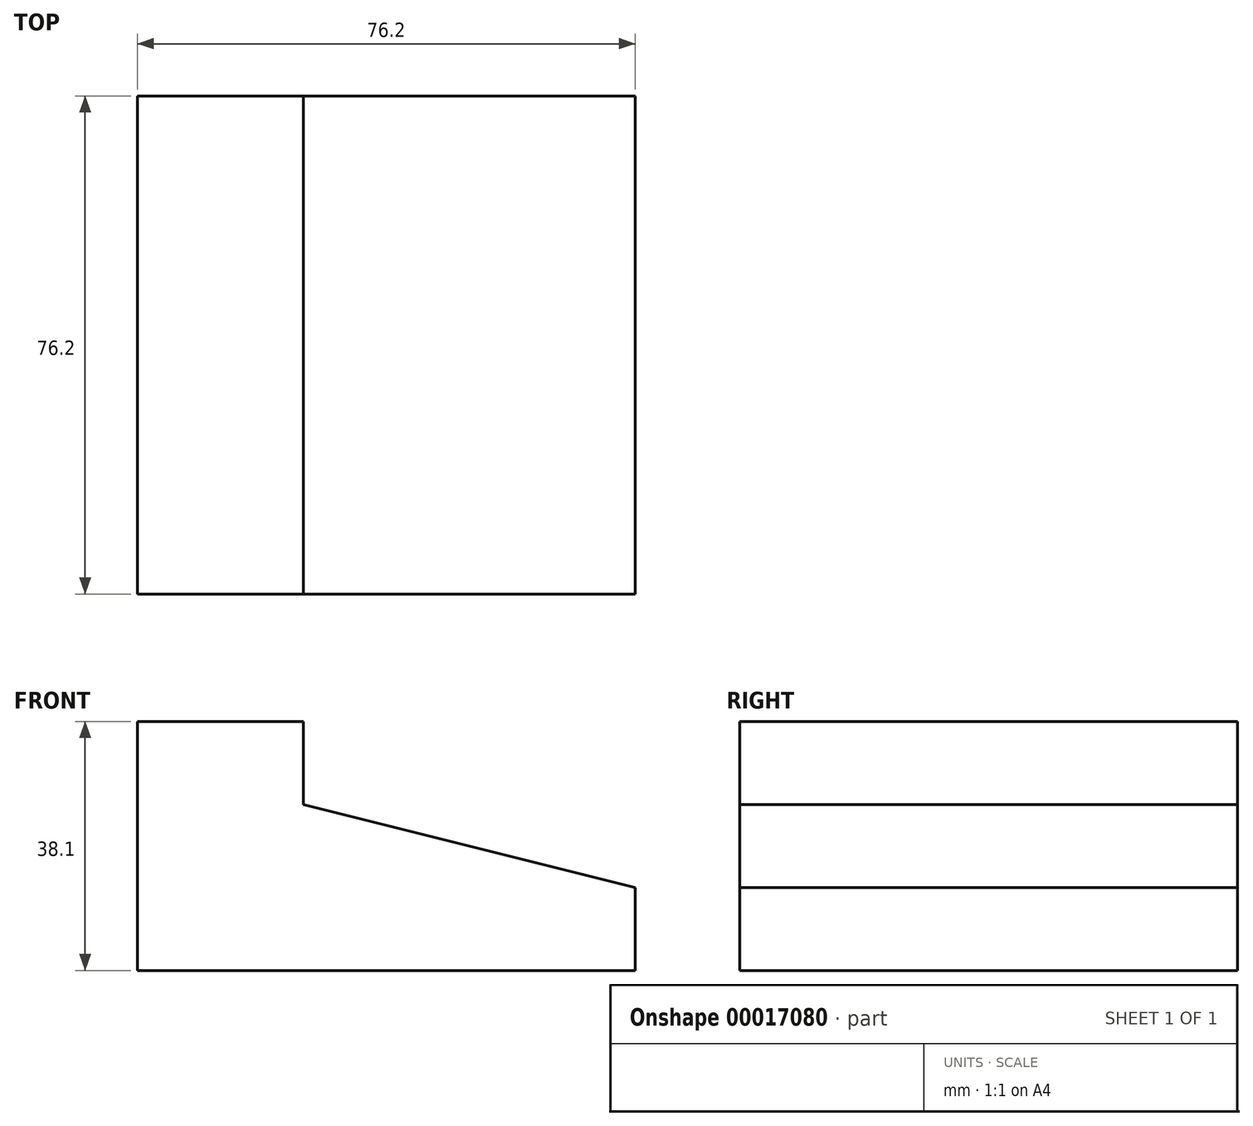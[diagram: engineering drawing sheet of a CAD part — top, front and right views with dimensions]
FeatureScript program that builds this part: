
annotation { "Feature Type Name" : "Feature", "Feature Type Description" : "" }
export const myFeature = defineFeature(function(context is Context, id is Id, definition is map)
    precondition{}
    {
        {
            var Q0;
            Q0=qCreatedBy(makeId("Front.planeOp"),FACE);
            var sketch = newSketch(context, id + "F0", { "sketchPlane" : qUnion([Q0])});
            skLineSegment(sketch, "E0", {"start": v(-76.2, 22.74) * mm, "end": v(-76.2, -15.36) * mm});
            skLineSegment(sketch, "E1", {"start": v(-76.2, -15.36) * mm, "end": v(0, -15.36) * mm});
            skLineSegment(sketch, "E2", {"start": v(0, -15.36) * mm, "end": v(0, -2.66) * mm});
            skLineSegment(sketch, "E3", {"start": v(-76.2, 22.74) * mm, "end": v(-50.8, 22.74) * mm});
            skLineSegment(sketch, "E4", {"start": v(-50.8, 22.74) * mm, "end": v(-50.8, 10.04) * mm});
            skLineSegment(sketch, "E5", {"start": v(-50.8, 10.04) * mm, "end": v(0, -2.66) * mm});
            skSolve(sketch);
        }
        {
            var Q0;
            Q0 = qSketchRegion(id + "F0", true);
            extrude(context, id + "F1", {"entities" : qUnion([Q0]), "oppositeDirection" : true, "depth" : 76.2 * mm});
        }
    });
